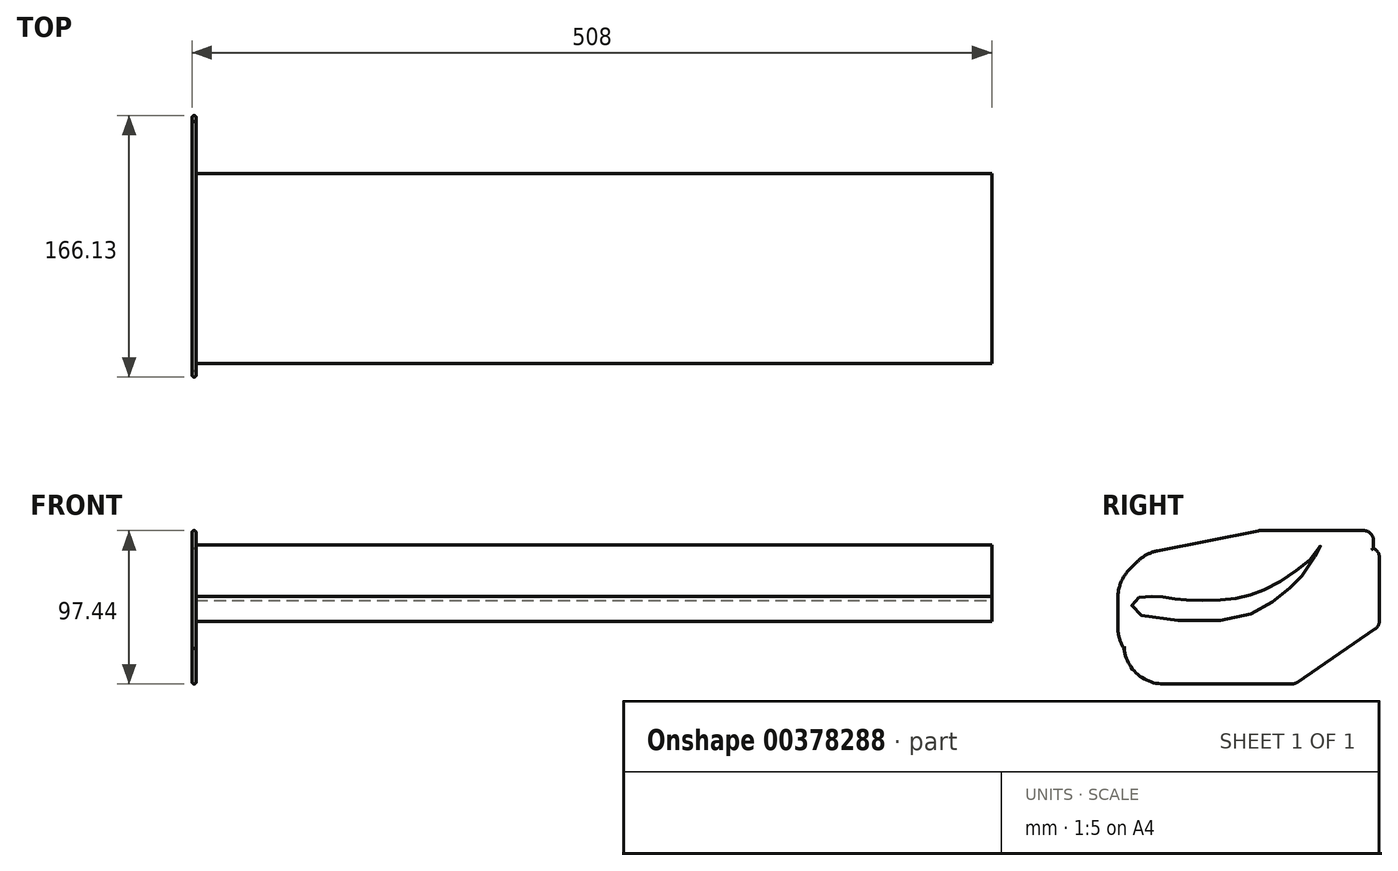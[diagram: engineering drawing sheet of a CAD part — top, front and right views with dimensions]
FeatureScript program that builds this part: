
annotation { "Feature Type Name" : "Feature", "Feature Type Description" : "" }
export const myFeature = defineFeature(function(context is Context, id is Id, definition is map)
    precondition{}
    {
        {
            var Q0;
            Q0=qCreatedBy(makeId("Right.planeOp"),FACE);
            var sketch = newSketch(context, id + "F0", { "sketchPlane" : qUnion([Q0])});
            skLineSegment(sketch, "E0.top", {"start": v(-60.5, -35.12) * mm, "end": v(20.88, -35.12) * mm});
            skLineSegment(sketch, "E0.left", {"start": v(-85.9, 8.94) * mm, "end": v(-85.9, -9.72) * mm});
            skLineSegment(sketch, "E0.right", {"start": v(76.52, 38.38) * mm, "end": v(76.52, 4.98) * mm});
            skLineSegment(sketch, "E1", {"start": v(-78.57, 26.78) * mm, "end": v(-73.72, 31.7) * mm});
            skLineSegment(sketch, "E2", {"start": v(76.52, 38.38) * mm, "end": v(76.52, 45.27) * mm});
            skLineSegment(sketch, "E3", {"start": v(-60.6, 38.76) * mm, "end": v(3.38, 51.5) * mm});
            skLineSegment(sketch, "E4", {"start": v(73.76, -0.26) * mm, "end": v(24.47, -34.01) * mm});
            skPoint(sketch, "E5.orphan", {"position": v(76.52, -35.12) * mm});
            skLineSegment(sketch, "E6", {"start": v(4.62, 51.62) * mm, "end": v(70.17, 51.62) * mm});
            skPoint(sketch, "E7.visualSharp", {"position": v(76.52, 51.62) * mm});
            skArc(sketch, "E7.filletArc", {"start": v(76.52, 45.27) * mm, "mid": v(74.66, 49.76) * mm, "end": v(70.17, 51.62) * mm});
            skPoint(sketch, "E8.visualSharp", {"position": v(76.52, 1.63) * mm});
            skArc(sketch, "E8.filletArc", {"start": v(73.76, -0.26) * mm, "mid": v(75.79, 2.01) * mm, "end": v(76.52, 4.98) * mm});
            skPoint(sketch, "E9.visualSharp", {"position": v(22.85, -35.12) * mm});
            skArc(sketch, "E9.filletArc", {"start": v(20.88, -35.12) * mm, "mid": v(22.76, -34.84) * mm, "end": v(24.47, -34.01) * mm});
            skPoint(sketch, "E10.visualSharp", {"position": v(4, 51.62) * mm});
            skArc(sketch, "E10.filletArc", {"start": v(4.62, 51.62) * mm, "mid": v(4, 51.6) * mm, "end": v(3.38, 51.5) * mm});
            skPoint(sketch, "E11.visualSharp", {"position": v(-85.9, -35.12) * mm});
            skArc(sketch, "E11.filletArc", {"start": v(-85.9, -28.77) * mm, "mid": v(-84.03, -33.26) * mm, "end": v(-79.54, -35.12) * mm});
            skPoint(sketch, "E12.visualSharp", {"position": v(-68.25, 37.24) * mm});
            skArc(sketch, "E12.filletArc", {"start": v(-60.6, 38.76) * mm, "mid": v(-67.7, 36.2) * mm, "end": v(-73.72, 31.7) * mm});
            skPoint(sketch, "E13.visualSharp", {"position": v(-85.9, 19.36) * mm});
            skArc(sketch, "E13.filletArc", {"start": v(-78.57, 26.78) * mm, "mid": v(-84, 18.58) * mm, "end": v(-85.9, 8.94) * mm});
            skArc(sketch, "E14.filletArc", {"start": v(-85.9, -9.72) * mm, "mid": v(-78.45, -27.68) * mm, "end": v(-60.5, -35.12) * mm});
            skLineSegment(sketch, "E15.top", {"start": v(-56.78, -45.82) * mm, "end": v(24.6, -45.82) * mm});
            skLineSegment(sketch, "E15.left", {"start": v(-82.18, -1.76) * mm, "end": v(-82.18, -20.42) * mm});
            skLineSegment(sketch, "E15.right", {"start": v(80.24, 27.68) * mm, "end": v(80.24, -5.72) * mm});
            skLineSegment(sketch, "E16", {"start": v(-74.85, 16.08) * mm, "end": v(-70, 21) * mm});
            skLineSegment(sketch, "E17", {"start": v(80.24, 27.68) * mm, "end": v(80.24, 34.58) * mm});
            skLineSegment(sketch, "E18", {"start": v(-56.9, 28.06) * mm, "end": v(7.1, 40.8) * mm});
            skLineSegment(sketch, "E19", {"start": v(77.47, -10.96) * mm, "end": v(28.19, -44.7) * mm});
            skPoint(sketch, "E20.orphan", {"position": v(80.24, -45.82) * mm});
            skLineSegment(sketch, "E21", {"start": v(8.34, 40.93) * mm, "end": v(73.89, 40.93) * mm});
            skPoint(sketch, "E22.visualSharp", {"position": v(80.24, 40.93) * mm});
            skArc(sketch, "E22.filletArc", {"start": v(80.24, 34.58) * mm, "mid": v(78.38, 39.07) * mm, "end": v(73.89, 40.93) * mm});
            skPoint(sketch, "E23.visualSharp", {"position": v(80.24, -9.07) * mm});
            skArc(sketch, "E23.filletArc", {"start": v(77.47, -10.96) * mm, "mid": v(79.5, -8.68) * mm, "end": v(80.24, -5.72) * mm});
            skPoint(sketch, "E24.visualSharp", {"position": v(26.57, -45.82) * mm});
            skArc(sketch, "E24.filletArc", {"start": v(24.6, -45.82) * mm, "mid": v(26.48, -45.53) * mm, "end": v(28.19, -44.7) * mm});
            skPoint(sketch, "E25.visualSharp", {"position": v(7.71, 40.93) * mm});
            skArc(sketch, "E25.filletArc", {"start": v(8.34, 40.93) * mm, "mid": v(7.71, 40.9) * mm, "end": v(7.1, 40.8) * mm});
            skPoint(sketch, "E26.visualSharp", {"position": v(-82.18, -45.82) * mm});
            skArc(sketch, "E26.filletArc", {"start": v(-82.18, -39.47) * mm, "mid": v(-80.32, -43.96) * mm, "end": v(-75.83, -45.82) * mm});
            skPoint(sketch, "E27.visualSharp", {"position": v(-64.53, 26.54) * mm});
            skArc(sketch, "E27.filletArc", {"start": v(-56.9, 28.06) * mm, "mid": v(-63.98, 25.5) * mm, "end": v(-70, 21) * mm});
            skPoint(sketch, "E28.visualSharp", {"position": v(-82.18, 8.66) * mm});
            skArc(sketch, "E28.filletArc", {"start": v(-74.85, 16.08) * mm, "mid": v(-80.28, 7.88) * mm, "end": v(-82.18, -1.76) * mm});
            skArc(sketch, "E29.filletArc", {"start": v(-82.18, -20.42) * mm, "mid": v(-74.74, -38.38) * mm, "end": v(-56.78, -45.82) * mm});
            skSolve(sketch);
        }
        {
            var Q0;
            Q0 = qSketchRegion(id + "F0", true);
            extrude(context, id + "F1", {"entities" : qUnion([Q0]), "depth" : 2.54 * mm});
        }
        {
            var Q0;
            Q0=makeQuery(id+"F1.opExtrude","CAP_FACE",FACE,{"disambiguationData":[OSD([sQuery(id+"F0.wireOp",EDGE,"E0.top"),sQuery(id+"F0.wireOp",EDGE,"E0.left"),sQuery(id+"F0.wireOp",EDGE,"E0.right"),sQuery(id+"F0.wireOp",EDGE,"E1"),sQuery(id+"F0.wireOp",EDGE,"E2"),sQuery(id+"F0.wireOp",EDGE,"E3"),sQuery(id+"F0.wireOp",EDGE,"E4"),sQuery(id+"F0.wireOp",EDGE,"E6"),sQuery(id+"F0.wireOp",EDGE,"E7.filletArc"),sQuery(id+"F0.wireOp",EDGE,"E8.filletArc"),sQuery(id+"F0.wireOp",EDGE,"E9.filletArc"),sQuery(id+"F0.wireOp",EDGE,"E10.filletArc"),sQuery(id+"F0.wireOp",EDGE,"E12.filletArc"),sQuery(id+"F0.wireOp",EDGE,"E13.filletArc"),sQuery(id+"F0.wireOp",EDGE,"E14.filletArc")])],"isStart":false});
            var Q1;
            Q1=makeQuery(id+"F1.opExtrude","CAP_FACE",FACE,{"disambiguationData":[OSD([sQuery(id+"F0.wireOp",EDGE,"E0.top"),sQuery(id+"F0.wireOp",EDGE,"E0.left"),sQuery(id+"F0.wireOp",EDGE,"E0.right"),sQuery(id+"F0.wireOp",EDGE,"E1"),sQuery(id+"F0.wireOp",EDGE,"E2"),sQuery(id+"F0.wireOp",EDGE,"E3"),sQuery(id+"F0.wireOp",EDGE,"E4"),sQuery(id+"F0.wireOp",EDGE,"E6"),sQuery(id+"F0.wireOp",EDGE,"E7.filletArc"),sQuery(id+"F0.wireOp",EDGE,"E8.filletArc"),sQuery(id+"F0.wireOp",EDGE,"E9.filletArc"),sQuery(id+"F0.wireOp",EDGE,"E10.filletArc"),sQuery(id+"F0.wireOp",EDGE,"E12.filletArc"),sQuery(id+"F0.wireOp",EDGE,"E13.filletArc"),sQuery(id+"F0.wireOp",EDGE,"E14.filletArc")])],"isStart":true});
            fillet(context, id + "F2", {"entities" : qUnion([Q0, Q1]), "radius" : 1.27 * mm, "tangentPropagation" : true, "allowEdgeOverflow" : false});
        }
        {
            var Q0;
            Q0=qCreatedBy(makeId("Right.planeOp"),FACE);
            var sketch = newSketch(context, id + "F3", { "sketchPlane" : qUnion([Q0])});
            skFitSpline(sketch, "E30", {"points": [v(-20.62, -5.36) * mm, v(-75.82, 0) * mm, v(-76.75, 4.65) * mm, v(-73.5, 8.6) * mm, v(-67.68, 9.77) * mm, v(-60.7, 9.77) * mm, v(-56.29, 9.3) * mm, v(-50, 8.37) * mm, v(-44.42, 7.68) * mm, v(-36.98, 7.21) * mm, v(-22.8, 7.44) * mm, v(-13.02, 8.14) * mm, v(-3.02, 10.23) * mm, v(4.19, 12.8) * mm, v(16.28, 18.6) * mm, v(29.07, 27.21) * mm, v(38.14, 35.35) * mm, v(43.26, 42.33) * mm, v(34.2, 27.21) * mm, v(26.05, 17.68) * mm, v(10, 4.65) * mm, v(-20.62, -5.36) * mm]});
            skPoint(sketch, "E31", {"position": v(12.33, 7.44) * mm});
            skSolve(sketch);
        }
        {
            var Q0;
            Q0 = qSketchRegion(id + "F3", true);
            extrude(context, id + "F4", {"entities" : qUnion([Q0]), "operationType" : NewBodyOperationType.ADD, "depth" : 508 * mm});
        }
    });
